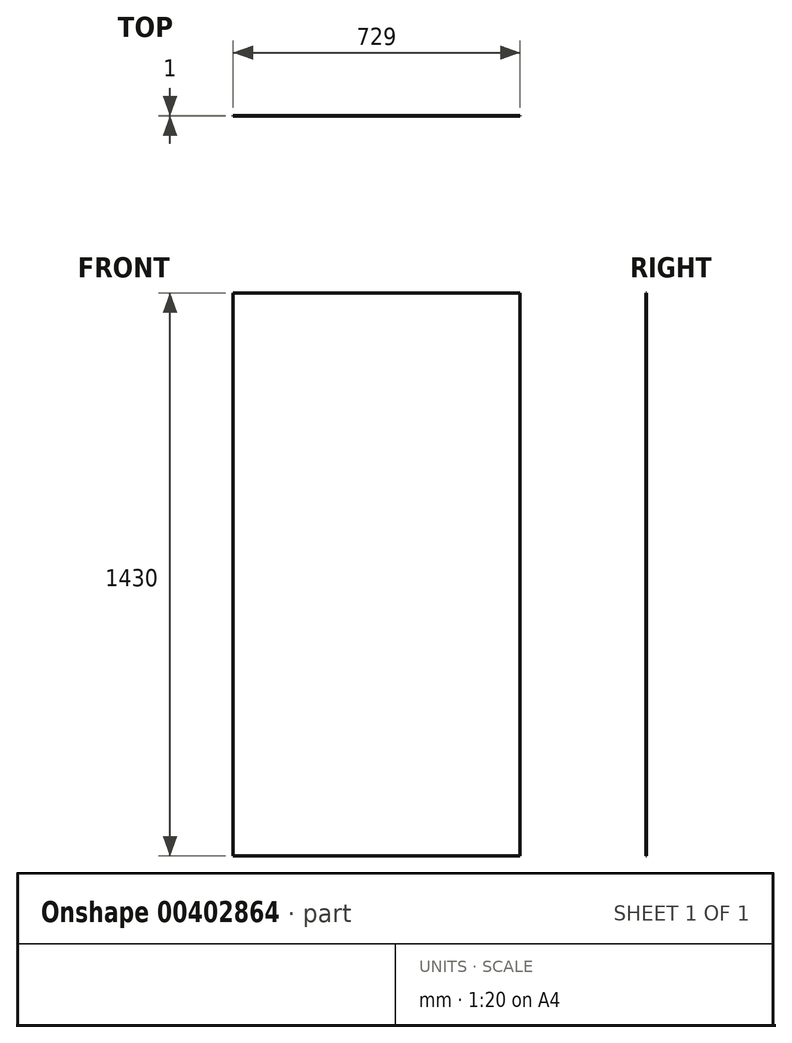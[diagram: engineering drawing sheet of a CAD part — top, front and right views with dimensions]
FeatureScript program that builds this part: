
annotation { "Feature Type Name" : "Feature", "Feature Type Description" : "" }
export const myFeature = defineFeature(function(context is Context, id is Id, definition is map)
    precondition{}
    {
        {
            var Q0;
            Q0=qCreatedBy(makeId("Front.planeOp"),FACE);
            var sketch = newSketch(context, id + "F0", { "sketchPlane" : qUnion([Q0])});
            skLineSegment(sketch, "E0.bottom", {"start": v(-364.5, 715) * mm, "end": v(364.5, 715) * mm});
            skLineSegment(sketch, "E0.top", {"start": v(-364.5, -715) * mm, "end": v(364.5, -715) * mm});
            skLineSegment(sketch, "E0.left", {"start": v(-364.5, 715) * mm, "end": v(-364.5, -715) * mm});
            skLineSegment(sketch, "E0.right", {"start": v(364.5, 715) * mm, "end": v(364.5, -715) * mm});
            skPoint(sketch, "E0.middle", {"position": v(0, 0) * mm});
            skSolve(sketch);
        }
        {
            var Q0;
            Q0=makeQuery(id+"F0.imprint","IMPRINT",FACE,{"disambiguationData":[TD([[makeQuery(id+"F0.imprint","IMPRINT",EDGE,{"derivedFrom":sQuery(id+"F0.wireOp",EDGE,"E0.bottom")}),-1.0]])]});
            extrude(context, id + "F1", {"entities" : qUnion([Q0]), "depth" : 1 * mm});
        }
    });
